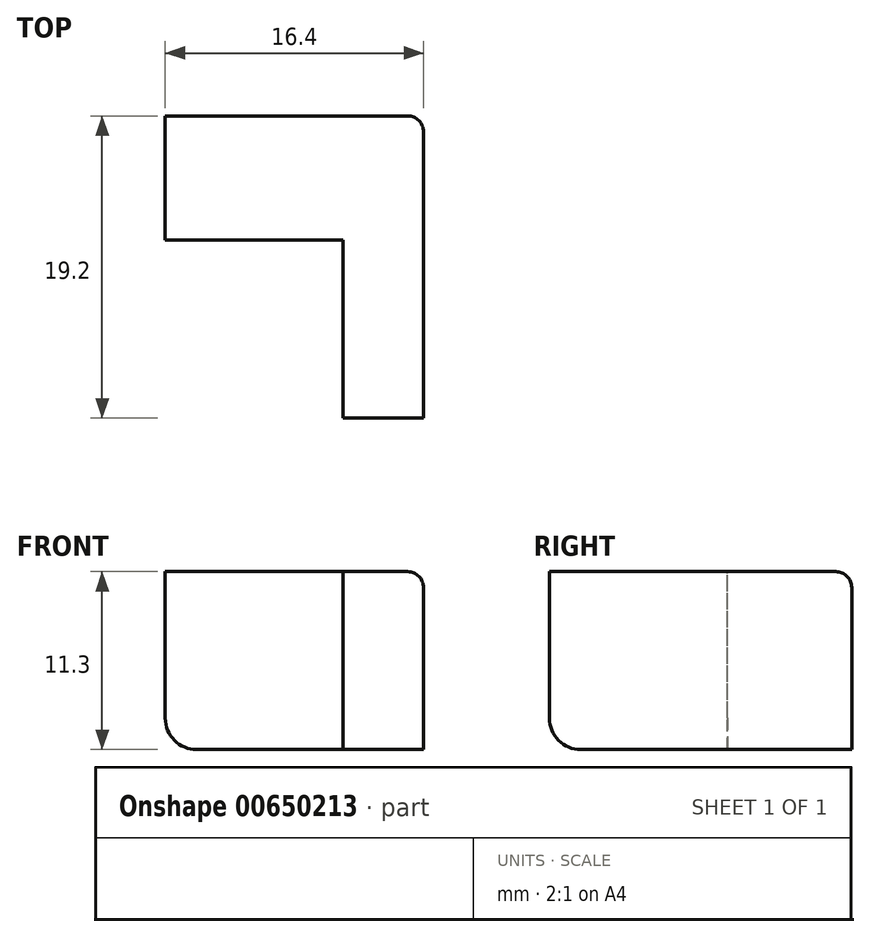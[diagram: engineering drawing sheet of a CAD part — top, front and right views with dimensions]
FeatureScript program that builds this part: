
annotation { "Feature Type Name" : "Feature", "Feature Type Description" : "" }
export const myFeature = defineFeature(function(context is Context, id is Id, definition is map)
    precondition{}
    {
        {
            var Q0;
            Q0=qCreatedBy(makeId("Top.planeOp"),FACE);
            var sketch = newSketch(context, id + "F0", { "sketchPlane" : qUnion([Q0])});
            skLineSegment(sketch, "E0.bottom", {"start": v(0, 0) * mm, "end": v(16.4, 0) * mm});
            skLineSegment(sketch, "E0.top", {"start": v(0, 19.2) * mm, "end": v(16.4, 19.2) * mm});
            skLineSegment(sketch, "E0.left", {"start": v(0, 0) * mm, "end": v(0, 19.2) * mm});
            skLineSegment(sketch, "E0.right", {"start": v(16.4, 0) * mm, "end": v(16.4, 19.2) * mm});
            skSolve(sketch);
        }
        {
            var Q0;
            Q0=makeQuery(id+"F0.imprint","IMPRINT",FACE,{"disambiguationData":[TD([[makeQuery(id+"F0.imprint","IMPRINT",EDGE,{"derivedFrom":sQuery(id+"F0.wireOp",EDGE,"E0.bottom")}),1.0]])]});
            extrude(context, id + "F1", {"entities" : qUnion([Q0]), "depth" : 11.3 * mm, "offsetDistance" : 25 * mm});
        }
        {
            var Q0;
            Q0=makeQuery(id+"F1.opExtrude","CAP_FACE",FACE,{"disambiguationData":[OSD([sQuery(id+"F0.wireOp",EDGE,"E0.bottom"),sQuery(id+"F0.wireOp",EDGE,"E0.top"),sQuery(id+"F0.wireOp",EDGE,"E0.left"),sQuery(id+"F0.wireOp",EDGE,"E0.right")])],"isStart":false});
            var sketch = newSketch(context, id + "F2", { "sketchPlane" : qUnion([Q0])});
            skLineSegment(sketch, "E1.bottom", {"start": v(0, 0) * mm, "end": v(11.3, 0) * mm});
            skLineSegment(sketch, "E1.top", {"start": v(0, 11.3) * mm, "end": v(11.3, 11.3) * mm});
            skLineSegment(sketch, "E1.left", {"start": v(0, 0) * mm, "end": v(0, 11.3) * mm});
            skLineSegment(sketch, "E1.right", {"start": v(11.3, 0) * mm, "end": v(11.3, 11.3) * mm});
            skSolve(sketch);
        }
        {
            var Q0;
            Q0=makeQuery(id+"F2.imprint","IMPRINT",FACE,{"disambiguationData":[TD([[makeQuery(id+"F2.imprint","IMPRINT",EDGE,{"derivedFrom":sQuery(id+"F2.wireOp",EDGE,"E1.bottom")}),1.0]])]});
            extrude(context, id + "F3", {"entities" : qUnion([Q0]), "operationType" : NewBodyOperationType.REMOVE, "oppositeDirection" : true, "depth" : 25 * mm, "offsetDistance" : 25 * mm});
        }
        {
            var Q0;
            Q0=makeQuery(id+"F1.opExtrude","CAP_EDGE",EDGE,{"disambiguationData":[OSD([sQuery(id+"F0.wireOp",EDGE,"E0.bottom")])],"isStart":true});
            var Q1;
            Q1=makeQuery(id+"F1.opExtrude","CAP_EDGE",EDGE,{"disambiguationData":[OSD([sQuery(id+"F0.wireOp",EDGE,"E0.left")])],"isStart":true});
            fillet(context, id + "F4", {"entities" : qUnion([Q0, Q1]), "radius" : 2 * mm, "tangentPropagation" : true, "allowEdgeOverflow" : false});
        }
        {
            var Q0;
            Q0=makeQuery(id+"F1.opExtrude","CAP_EDGE",EDGE,{"disambiguationData":[OSD([sQuery(id+"F0.wireOp",EDGE,"E0.top")])],"isStart":false});
            var Q1;
            Q1=makeQuery(id+"F1.opExtrude","CAP_EDGE",EDGE,{"disambiguationData":[OSD([sQuery(id+"F0.wireOp",EDGE,"E0.right")])],"isStart":false});
            var Q2;
            Q2=makeQuery(id+"F1.opExtrude","SWEPT_EDGE",EDGE,{"disambiguationData":[OSD([sQuery(id+"F0.wireOp",EDGE,"E0.top"),sQuery(id+"F0.wireOp",EDGE,"E0.right")])]});
            fillet(context, id + "F5", {"entities" : qUnion([Q0, Q1, Q2]), "radius" : 1 * mm, "tangentPropagation" : true, "allowEdgeOverflow" : false});
        }
    });
